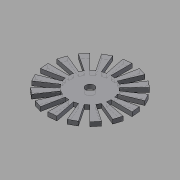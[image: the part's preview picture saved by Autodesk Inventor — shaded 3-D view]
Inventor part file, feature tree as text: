
AUTODESK INVENTOR PART (.ipt)
format: ipt  version: 2015 (Build 190159000, 159)  size: 174,080 bytes
history: native  units: in
note: dims shown in document units (in); Inventor stores cm internally (conversion verified against a paired STEP export)
features: other x3, sketch x1
ambient origin geometry x8: Origin, YZ Plane, XZ Plane, XY Plane, X Axis, Y Axis, Z Axis, Center Point
bodies: Solid1 (feature_tree)
feature tree (4):
  other  "encoder_MIR4.ipt"
  other  "Solid1::encoder_MIR4.ipt"
  other  "TaggingFeature1"
  sketch  "Sketch1"  dims[d0=0.3937in]
